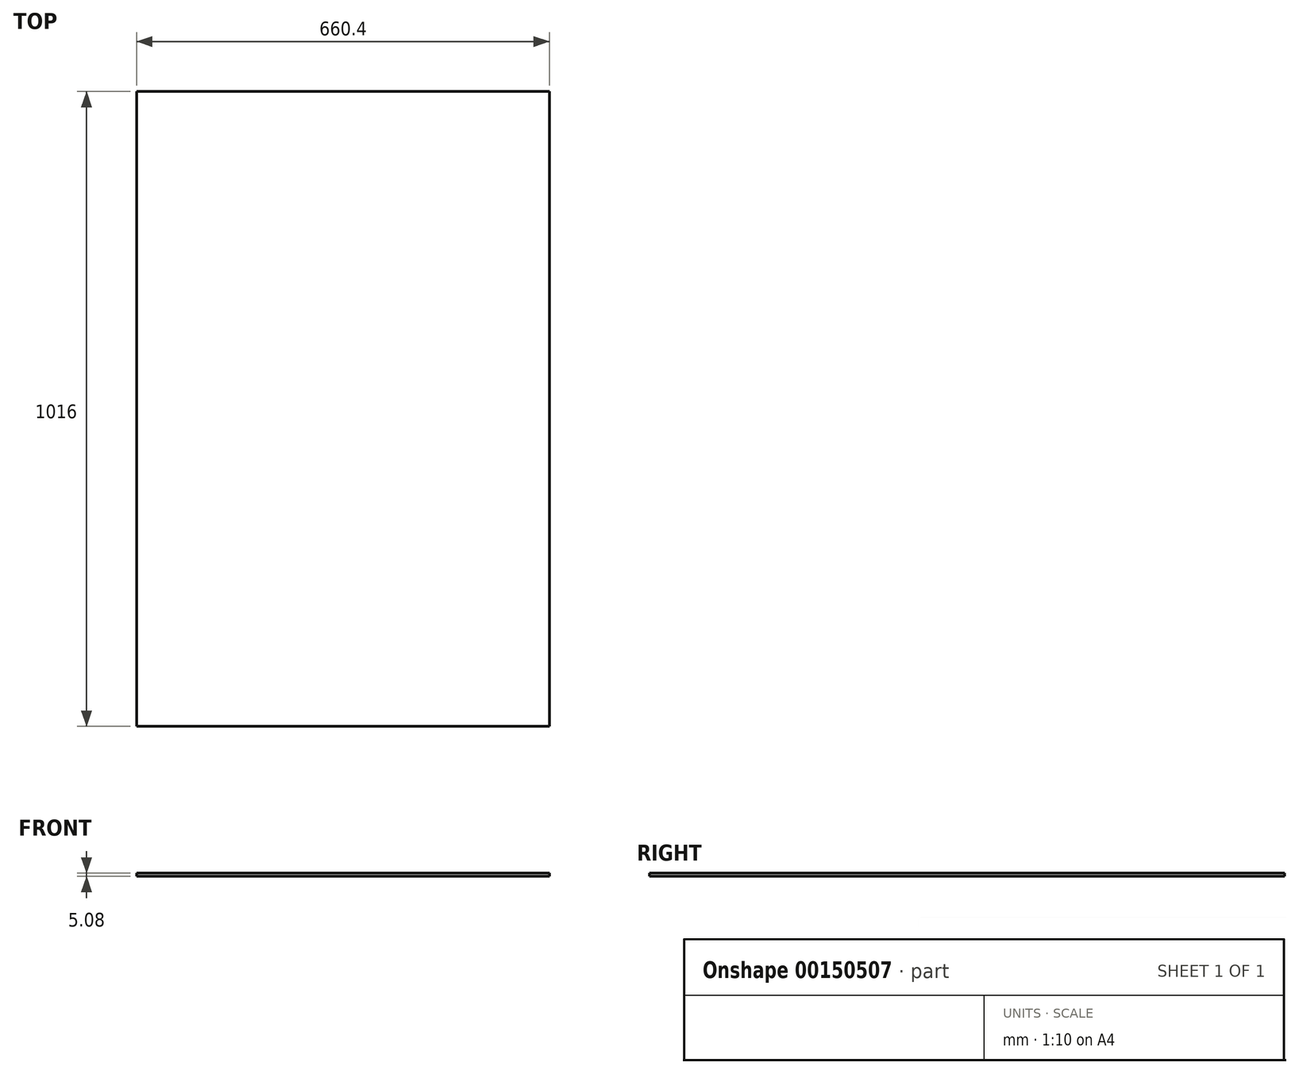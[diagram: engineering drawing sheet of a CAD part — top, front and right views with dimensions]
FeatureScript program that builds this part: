
annotation { "Feature Type Name" : "Feature", "Feature Type Description" : "" }
export const myFeature = defineFeature(function(context is Context, id is Id, definition is map)
    precondition{}
    {
        {
            var Q0;
            Q0=qCreatedBy(makeId("Top.planeOp"),FACE);
            var sketch = newSketch(context, id + "F0", { "sketchPlane" : qUnion([Q0])});
            skLineSegment(sketch, "E0.bottom", {"start": v(330.2, 508) * mm, "end": v(-330.2, 508) * mm});
            skLineSegment(sketch, "E0.top", {"start": v(330.2, -508) * mm, "end": v(-330.2, -508) * mm});
            skLineSegment(sketch, "E0.left", {"start": v(330.2, 508) * mm, "end": v(330.2, -508) * mm});
            skLineSegment(sketch, "E0.right", {"start": v(-330.2, 508) * mm, "end": v(-330.2, -508) * mm});
            skPoint(sketch, "E0.middle", {"position": v(0, 0) * mm});
            skPoint(sketch, "E1.middle", {"position": v(67.17, 508) * mm});
            skSolve(sketch);
        }
        {
            var Q0;
            {var subQ0=sQuery(id+"F0.wireOp",EDGE,"E0.top");Q0=makeQuery(id+"F0.imprint","IMPRINT",FACE,{"disambiguationData":[TD([[makeQuery(id+"F0.imprint","IMPRINT",EDGE,{"derivedFrom":subQ0}),-1.0]])]});}
            extrude(context, id + "F1", {"entities" : qUnion([Q0]), "oppositeDirection" : true, "depth" : 5.08 * mm});
        }
    });
